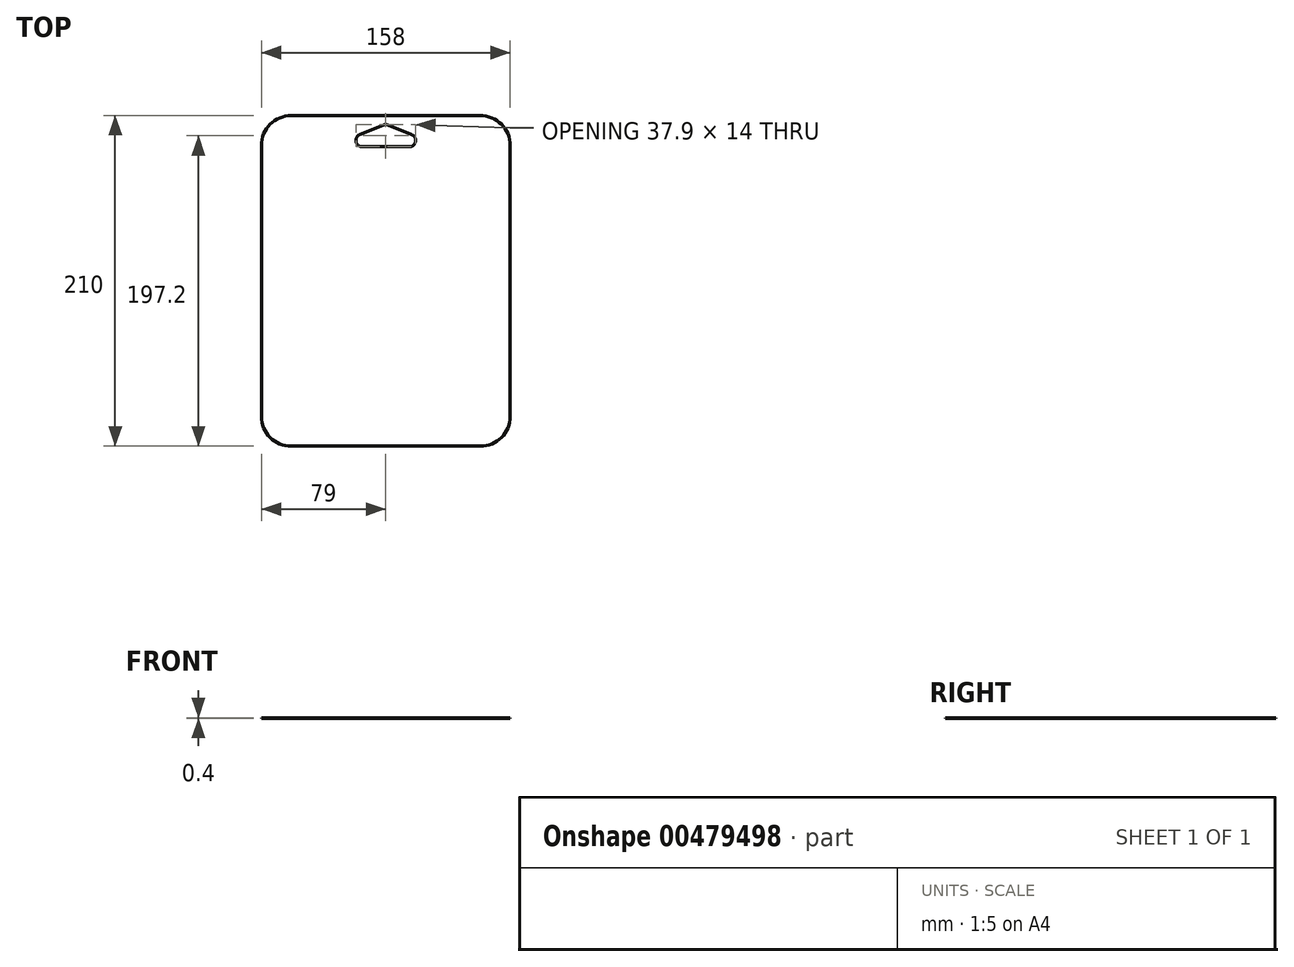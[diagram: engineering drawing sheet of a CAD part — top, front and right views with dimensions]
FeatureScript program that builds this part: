
annotation { "Feature Type Name" : "Feature", "Feature Type Description" : "" }
export const myFeature = defineFeature(function(context is Context, id is Id, definition is map)
    precondition{}
    {
        {
            var Q0;
            Q0=qCreatedBy(makeId("Top.planeOp"),FACE);
            var sketch = newSketch(context, id + "F0", { "sketchPlane" : qUnion([Q0])});
            skLineSegment(sketch, "E0", {"start": v(-15, 0) * mm, "end": v(15, 0) * mm});
            skArc(sketch, "E1", {"start": v(15, 0) * mm, "mid": v(18.93, 3.24) * mm, "end": v(16.49, 7.71) * mm});
            skArc(sketch, "E2", {"start": v(-16.49, 7.71) * mm, "mid": v(-18.93, 3.24) * mm, "end": v(-15, 0) * mm});
            skLineSegment(sketch, "E3", {"start": v(-16.49, 7.71) * mm, "end": v(-1.49, 13.71) * mm});
            skArc(sketch, "E4", {"start": v(1.49, 13.71) * mm, "mid": v(0, 14) * mm, "end": v(-1.49, 13.71) * mm});
            skLineSegment(sketch, "E5", {"start": v(16.49, 7.71) * mm, "end": v(1.49, 13.71) * mm});
            skLineSegment(sketch, "E6", {"start": v(-19, 14) * mm, "end": v(-19, -8.09) * mm, "construction": true});
            skLineSegment(sketch, "E7", {"start": v(19, 14) * mm, "end": v(19, -6.38) * mm, "construction": true});
            skLineSegment(sketch, "E8", {"start": v(-19, 14) * mm, "end": v(19, 14) * mm, "construction": true});
            skLineSegment(sketch, "E9", {"start": v(-79, 19.8) * mm, "end": v(79, 19.8) * mm});
            skLineSegment(sketch, "E10", {"start": v(79, 19.8) * mm, "end": v(79, -190.2) * mm});
            skLineSegment(sketch, "E11", {"start": v(79, -190.2) * mm, "end": v(-79, -190.2) * mm});
            skLineSegment(sketch, "E12", {"start": v(-79, -190.2) * mm, "end": v(-79, 19.8) * mm});
            skLineSegment(sketch, "E13", {"start": v(0, 19.8) * mm, "end": v(0, 0) * mm, "construction": true});
            skSolve(sketch);
        }
        {
            var Q0;
            Q0 = qSketchRegion(id + "F0", true);
            extrude(context, id + "F1", {"entities" : qUnion([Q0]), "endBound" : BoundingType.SYMMETRIC, "depth" : 0.4 * mm});
        }
        {
            var Q0;
            Q0=makeQuery(id+"F1.opExtrude","SWEPT_EDGE",EDGE,{"disambiguationData":[OSD([sQuery(id+"F0.wireOp",EDGE,"E9"),sQuery(id+"F0.wireOp",EDGE,"E10")])]});
            var Q1;
            Q1=makeQuery(id+"F1.opExtrude","SWEPT_EDGE",EDGE,{"disambiguationData":[OSD([sQuery(id+"F0.wireOp",EDGE,"E9"),sQuery(id+"F0.wireOp",EDGE,"E12")])]});
            var Q2;
            Q2=makeQuery(id+"F1.opExtrude","SWEPT_EDGE",EDGE,{"disambiguationData":[OSD([sQuery(id+"F0.wireOp",EDGE,"E10"),sQuery(id+"F0.wireOp",EDGE,"E11")])]});
            var Q3;
            Q3=makeQuery(id+"F1.opExtrude","SWEPT_EDGE",EDGE,{"disambiguationData":[OSD([sQuery(id+"F0.wireOp",EDGE,"E11"),sQuery(id+"F0.wireOp",EDGE,"E12")])]});
            fillet(context, id + "F2", {"entities" : qUnion([Q0, Q1, Q2, Q3]), "radius" : 19 * mm, "tangentPropagation" : true, "allowEdgeOverflow" : false});
        }
    });
